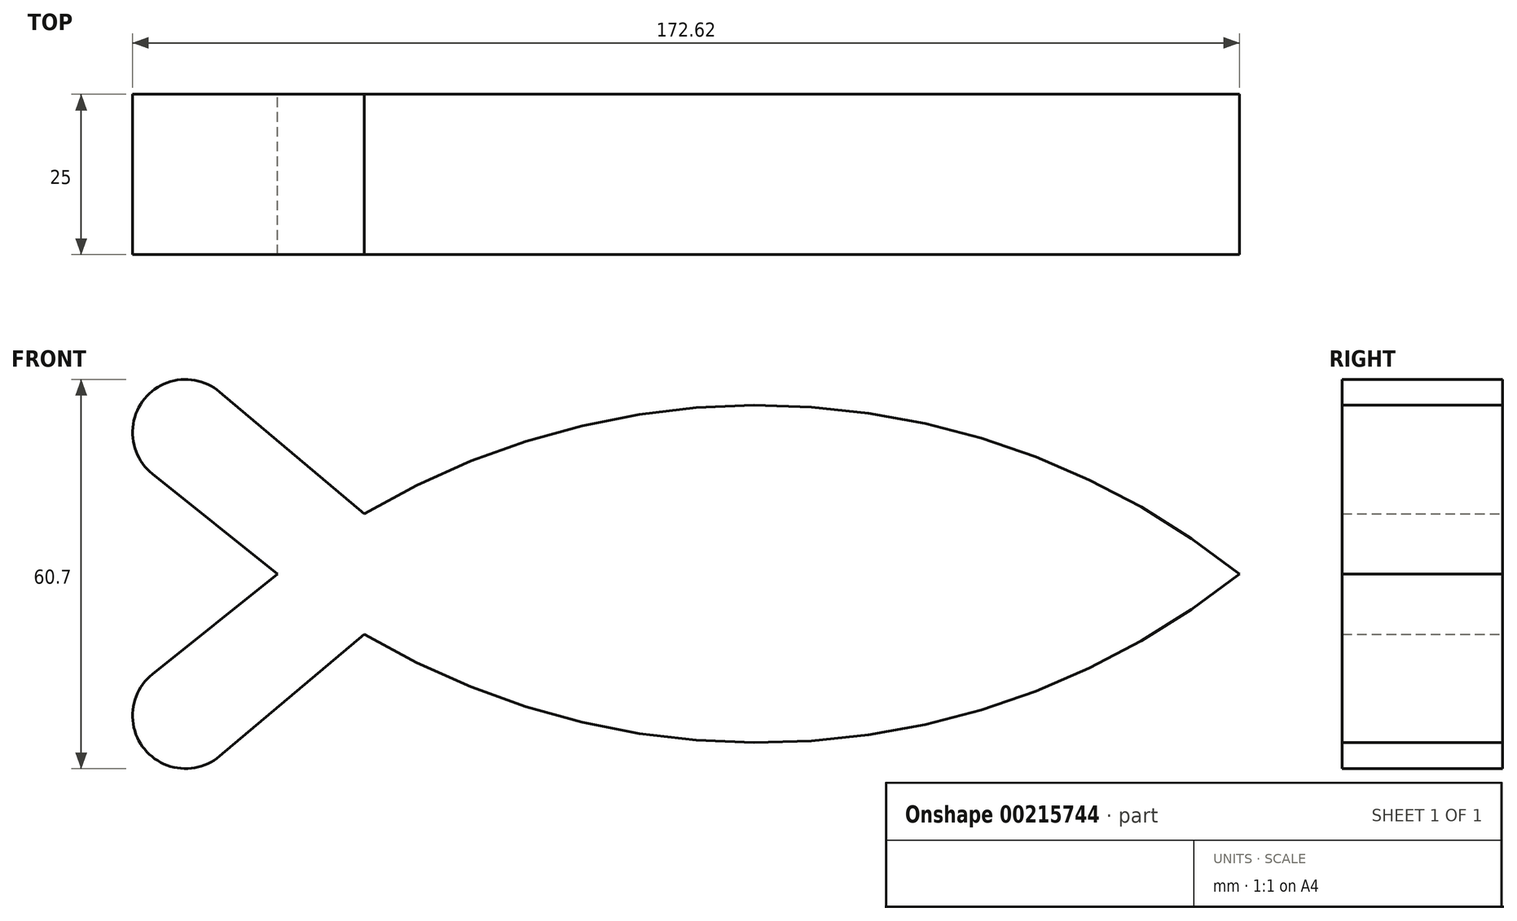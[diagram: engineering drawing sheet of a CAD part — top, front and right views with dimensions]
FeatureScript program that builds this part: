
annotation { "Feature Type Name" : "Feature", "Feature Type Description" : "" }
export const myFeature = defineFeature(function(context is Context, id is Id, definition is map)
    precondition{}
    {
        {
            var Q0;
            Q0=qCreatedBy(makeId("Front.planeOp"),FACE);
            var sketch = newSketch(context, id + "F0", { "sketchPlane" : qUnion([Q0])});
            skArc(sketch, "E0", {"start": v(150, 0) * mm, "mid": v(75, 26.33) * mm, "end": v(0, 0) * mm});
            skArc(sketch, "E1.MirrorCS", {"start": v(150, 0) * mm, "mid": v(75, -26.33) * mm, "end": v(0, 0) * mm});
            skLineSegment(sketch, "E2", {"start": v(0, 0) * mm, "end": v(-19.52, 15.62) * mm});
            skArc(sketch, "E3", {"start": v(-19.52, 15.62) * mm, "mid": v(-20.73, 27.34) * mm, "end": v(-9, 28.4) * mm});
            skLineSegment(sketch, "E4", {"start": v(-9, 28.4) * mm, "end": v(13.52, 9.38) * mm});
            skLineSegment(sketch, "E5.MirrorCS", {"start": v(-9, -28.4) * mm, "end": v(13.52, -9.38) * mm});
            skArc(sketch, "E6.MirrorCS", {"start": v(-19.52, -15.62) * mm, "mid": v(-20.73, -27.34) * mm, "end": v(-9, -28.4) * mm});
            skLineSegment(sketch, "E7.MirrorCS", {"start": v(0, 0) * mm, "end": v(-19.52, -15.62) * mm});
            skSolve(sketch);
        }
        {
            var Q0;
            Q0 = qSketchRegion(id + "F0", true);
            extrude(context, id + "F1", {"entities" : qUnion([Q0]), "depth" : 25 * mm});
        }
    });
